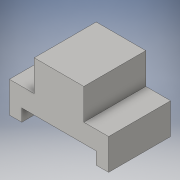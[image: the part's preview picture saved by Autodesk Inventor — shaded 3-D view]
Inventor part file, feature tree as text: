
AUTODESK INVENTOR PART (.ipt)
format: ipt  version: 2016 (Build 200138000, 138)  size: 116,736 bytes
history: native  units: in
note: dims shown in document units (in); Inventor stores cm internally (conversion verified against a paired STEP export)
features: extrude x3, sketch x3
ambient origin geometry x8: Origin, YZ Plane, XZ Plane, XY Plane, X Axis, Y Axis, Z Axis, Center Point
bodies: Solid1 (feature_tree)
feature tree (6):
  extrude  "Extrusion1"  Depth=1.25in
  extrude  "Extrusion2"  Depth=0.625in
  extrude  "Extrusion3"  Depth=0.625in
  sketch  "Sketch1"  dims[d0=2.0in d1=1.25in]
  sketch  "Sketch2"  dims[d2=1.25in d3=0.0in d4=0.625in]
  sketch  "Sketch3"  dims[d5=0.5in d6=0.625in d7=0.5in d8=1.25in d9=0.0in d10=0.25in d11=0.25in d12=0.25in d13=1.25in d14=0.0in]
